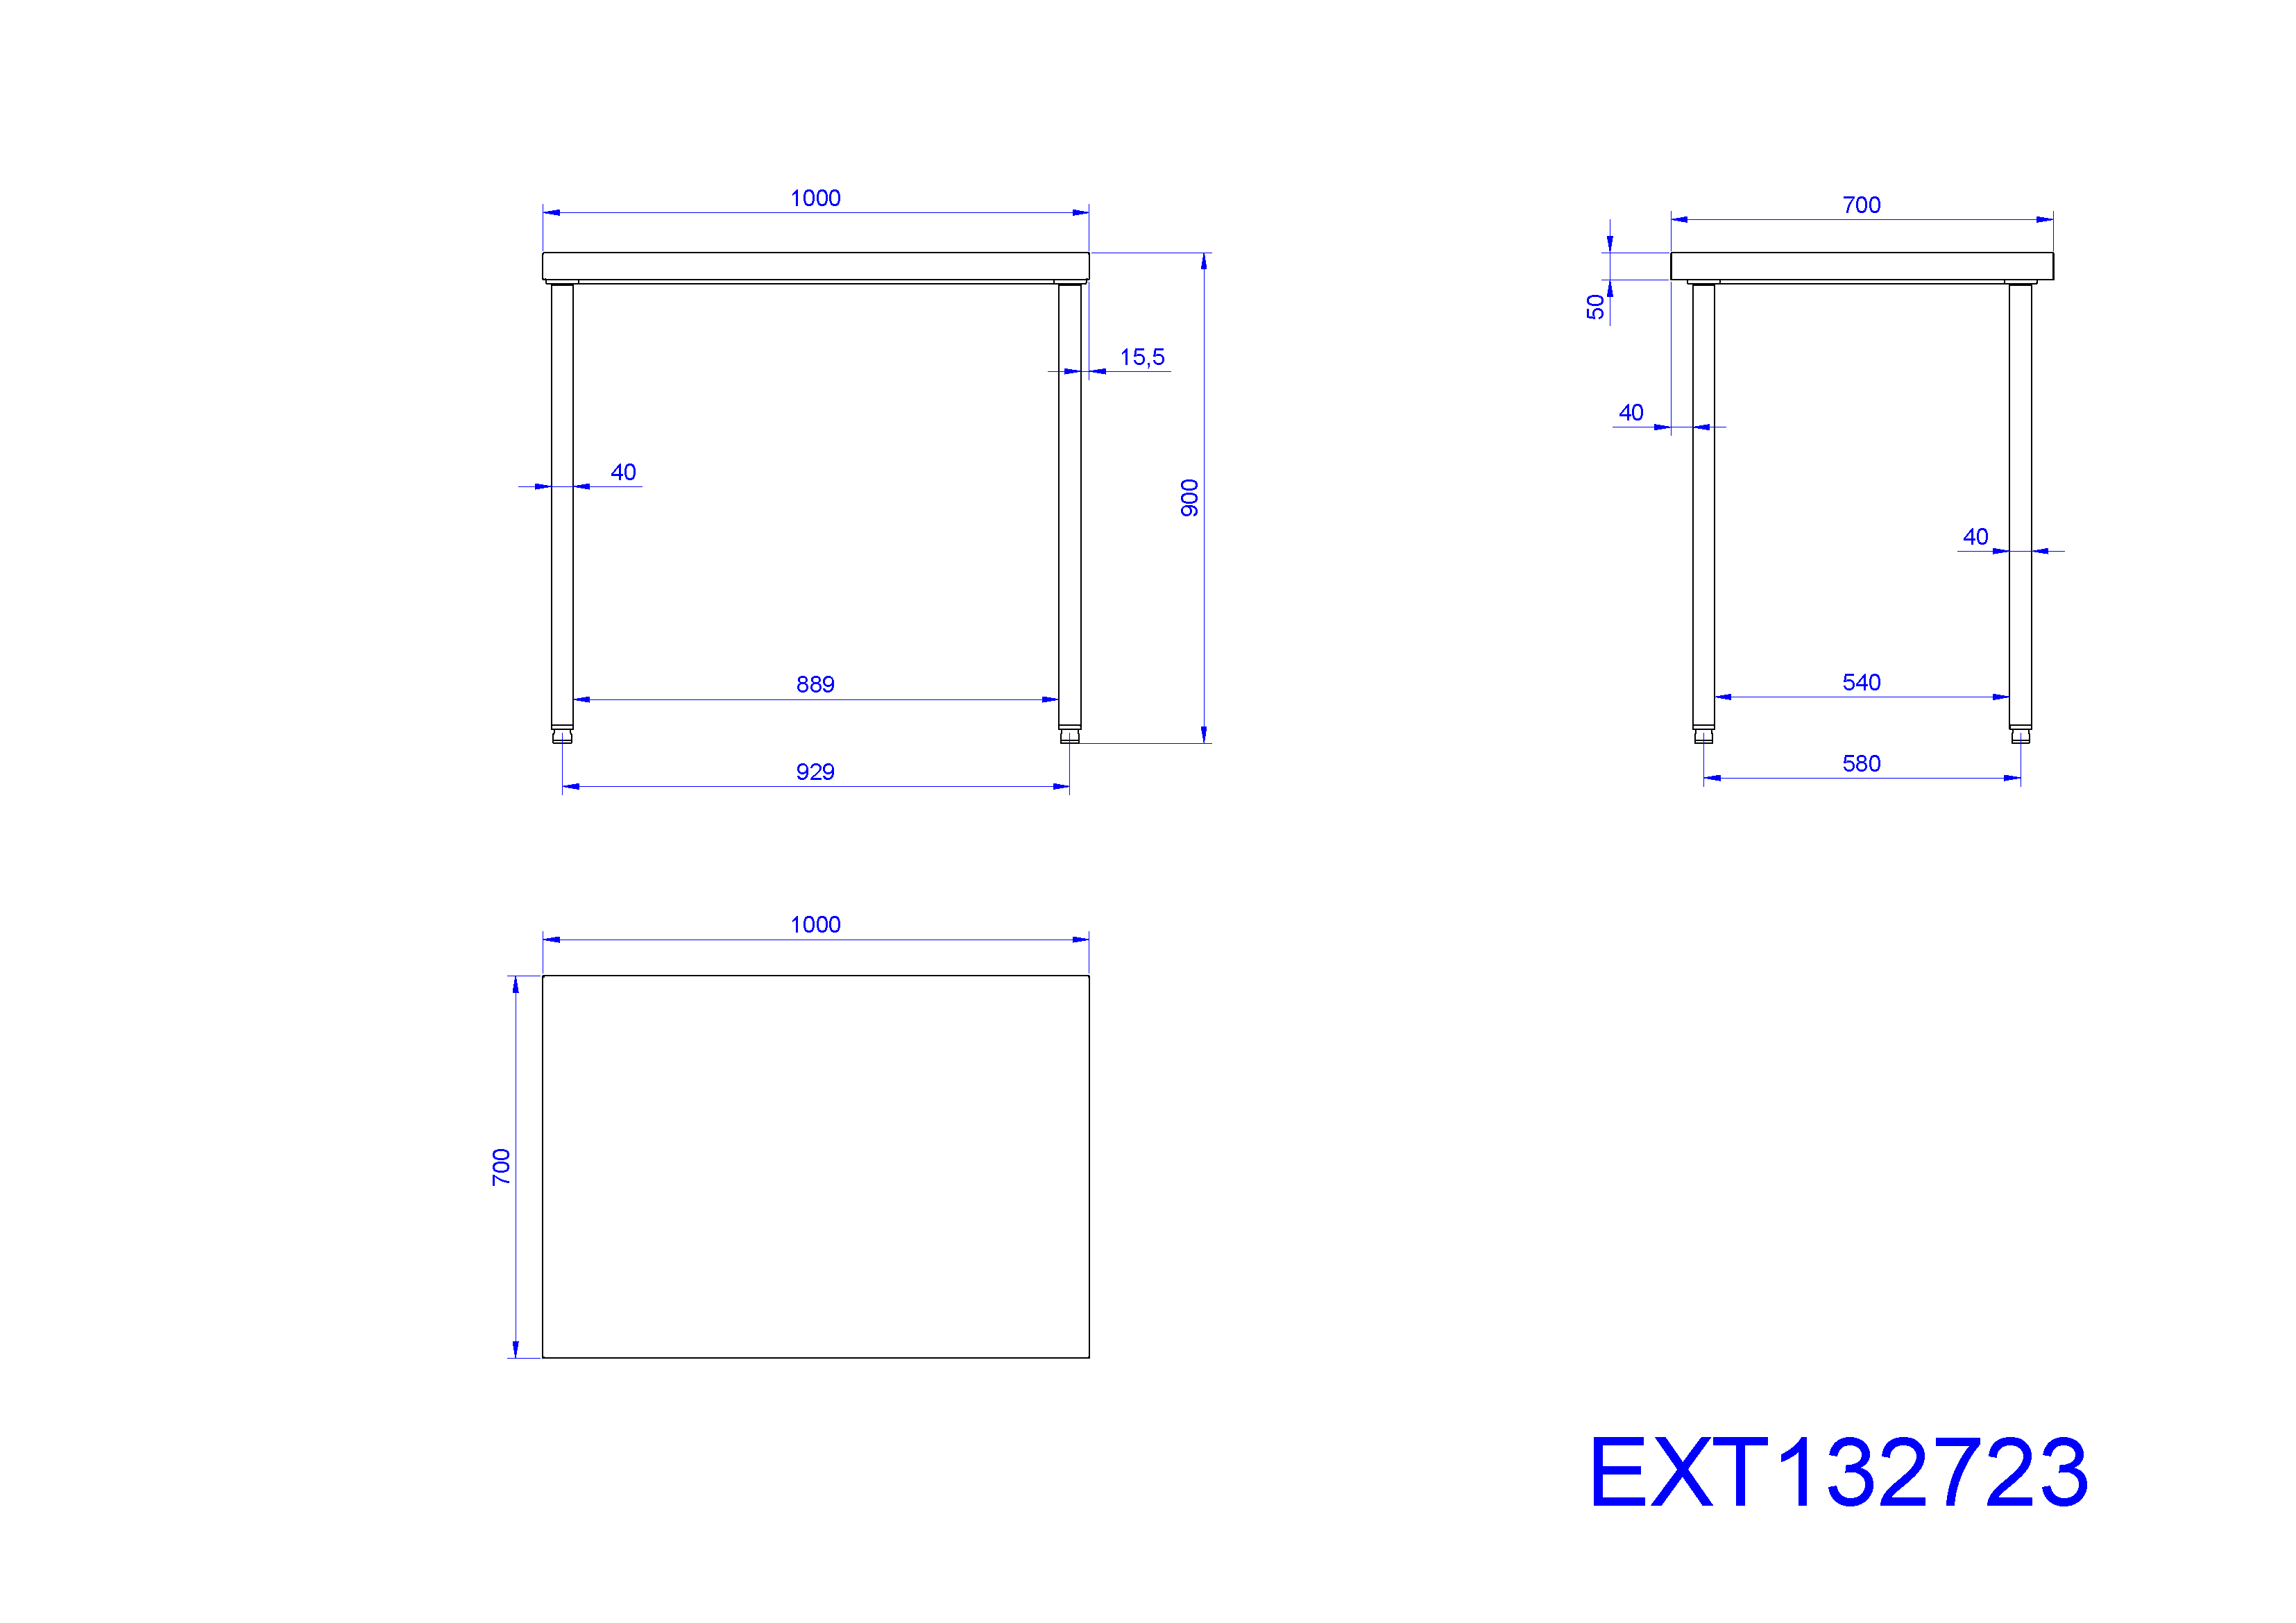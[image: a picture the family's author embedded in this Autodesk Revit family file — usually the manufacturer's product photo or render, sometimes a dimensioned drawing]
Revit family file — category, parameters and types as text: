
# Revit family: QF_ELECTROLUXPROFESSIONAL_132841_WTD1407N
name_source: partatom
category: Attrezzature speciali
units: mm (PartAtom-declared; Revit-internal decimal feet)

## family parameters
Basato su piano di lavoro = No
Condiviso = No
Punto di calcolo locali = No
Quota connettore circolare = Usa diametro
Sempre verticale = Sì
Taglio con vuoti quando caricato = No
Tipo di parte = Normale

## types (1)
- Standard
    Accessory = Sì
    Cold Water Size = 0 mm
    Compressed Air Pressure = 0.0 Pa
    Compressed Air Size = 0 mm
    Compressed Air Volume = 0.0 L/s
    Condensate Return Size = 0 mm
    Cycle = 0 Hz
    Depth Actual = 700 mm  [stored 2.29659 ft]
    Descrizione = WORK TABLE-DISASSEMBLED 1400MM
    Direct Waste Size = 0 mm
    Gas Input Pressure = 0
    Gas KW = 0
    Gas Size = 0 mm
    HP = 0 HP
    Height Actual = 900 mm  [stored 2.95276 ft]
    Hot Water Size = 0 mm
    Item Number = 132841
    Length Actual = 1400 mm  [stored 4.59318 ft]
    Modello = WTD1407N
    Phase = 0
    Produttore = Electrolux Professional
    Prospetto di default = 0 mm  [stored 0 ft]
    Refrigerant Compressor Remote = Sì
    Refrigeration Liquid Line Size = 0 mm  [stored 0 ft]
    Refrigeration Suction Line Size = 0 mm  [stored 0 ft]
    Steam Consumption per Hour = 0
    Steam Supply Maximum Pressure = 0.0 Pa
    Steam Supply Minimum Pressure = 0.0 Pa
    Steam Supply Size = 0 mm
    URL = https://www.electroluxprofessional.com
    URL Manufacturer = https://www.electroluxprofessional.com
    Volts = 0 V
    Watts = 0 W
    Weight = 47.00 kg

note: source unit labels omitted for Gas Input Pressure — the stored unit's dimension contradicts the parameter name (converter mislabeling)

note: [stored X ft] marks values corroborated as IEEE doubles in the binary element streams (Revit-internal decimal feet)

## geometry (parser evidence)
native form markers: Sweep x2
no freeform markers — native parametric forms only
